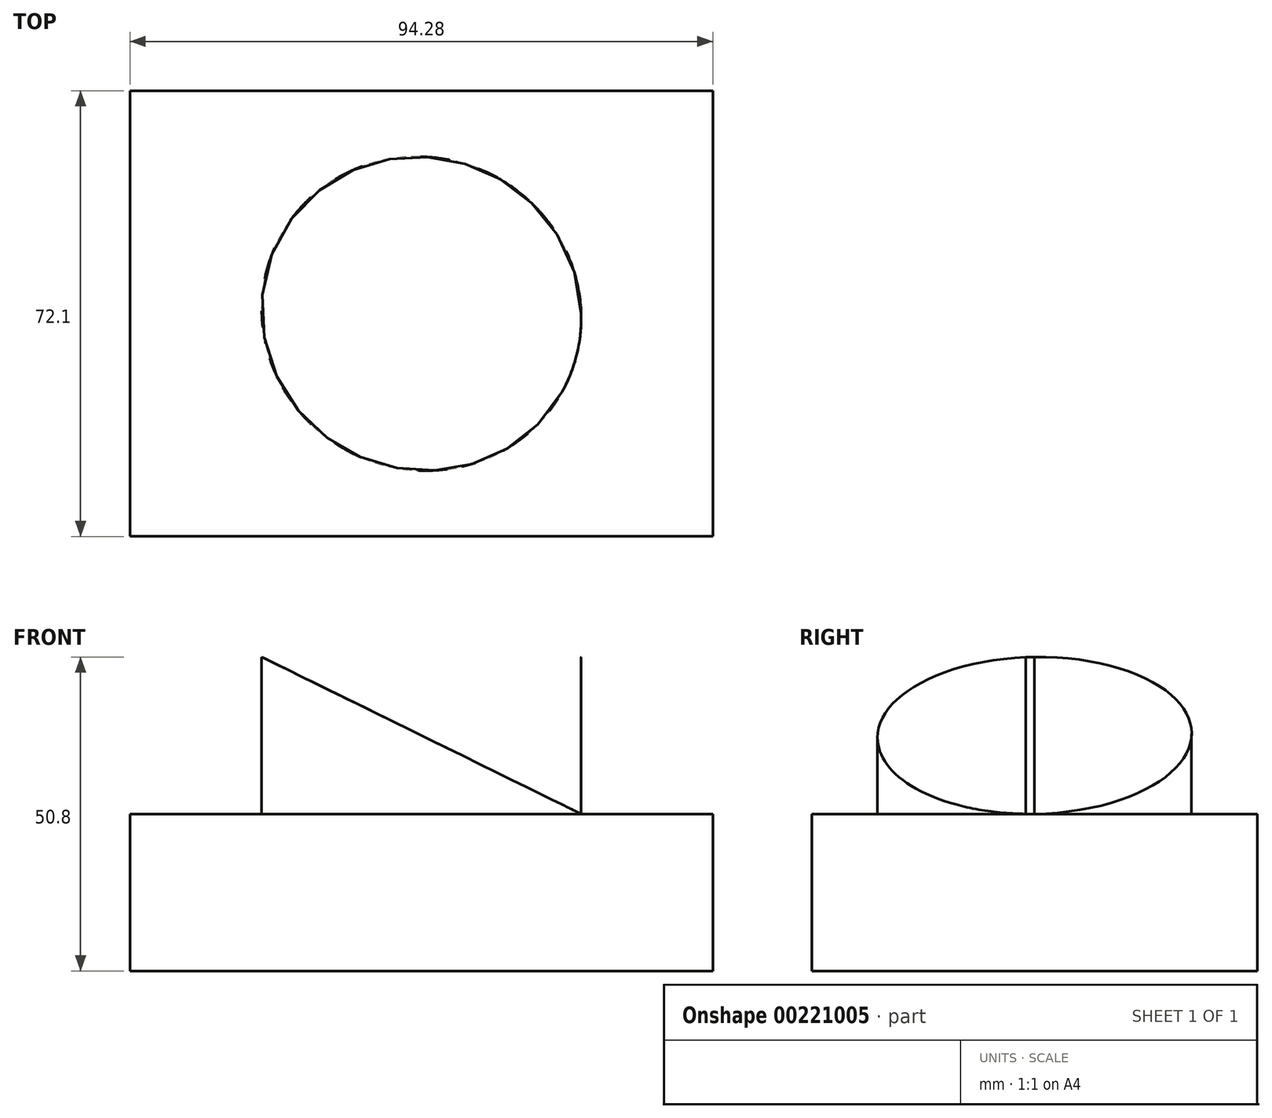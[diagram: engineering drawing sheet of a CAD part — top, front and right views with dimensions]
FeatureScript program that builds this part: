
annotation { "Feature Type Name" : "Feature", "Feature Type Description" : "" }
export const myFeature = defineFeature(function(context is Context, id is Id, definition is map)
    precondition{}
    {
        {
            var Q0;
            Q0=qCreatedBy(makeId("Top.planeOp"),FACE);
            var sketch = newSketch(context, id + "F0", { "sketchPlane" : qUnion([Q0])});
            skLineSegment(sketch, "E0.bottom", {"start": v(47.14, -36.05) * mm, "end": v(-47.14, -36.05) * mm});
            skLineSegment(sketch, "E0.top", {"start": v(47.14, 36.05) * mm, "end": v(-47.14, 36.05) * mm});
            skLineSegment(sketch, "E0.left", {"start": v(47.14, -36.05) * mm, "end": v(47.14, 36.05) * mm});
            skLineSegment(sketch, "E0.right", {"start": v(-47.14, -36.05) * mm, "end": v(-47.14, 36.05) * mm});
            skPoint(sketch, "E0.middle", {"position": v(0, 0) * mm});
            skSolve(sketch);
        }
        {
            var Q0;
            Q0 = qSketchRegion(id + "F0", true);
            extrude(context, id + "F1", {"entities" : qUnion([Q0]), "depth" : 25.4 * mm});
        }
        {
            var Q0;
            Q0=makeQuery(id+"F1.opExtrude","CAP_FACE",FACE,{"disambiguationData":[OSD([sQuery(id+"F0.wireOp",EDGE,"E0.bottom"),sQuery(id+"F0.wireOp",EDGE,"E0.top"),sQuery(id+"F0.wireOp",EDGE,"E0.left"),sQuery(id+"F0.wireOp",EDGE,"E0.right")])],"isStart":false});
            var sketch = newSketch(context, id + "F2", { "sketchPlane" : qUnion([Q0])});
            skEllipse(sketch, "E1", {"center": v(0, 0) * mm, "majorRadius": 26.04 * mm, "minorRadius": 25.2 * mm, "majorAxis": v(0.87, -0.49)});
            skSolve(sketch);
        }
        {
            var Q0;
            Q0 = qSketchRegion(id + "F2", true);
            extrude(context, id + "F3", {"entities" : qUnion([Q0]), "operationType" : NewBodyOperationType.ADD, "depth" : 25.4 * mm});
        }
        {
            var Q0;
            Q0=qCreatedBy(makeId("Front.planeOp"),FACE);
            var sketch = newSketch(context, id + "F4", { "sketchPlane" : qUnion([Q0])});
            skLineSegment(sketch, "E2.0", {"start": v(-25.85, 50.8) * mm, "end": v(25.85, 50.8) * mm});
            skLineSegment(sketch, "E3", {"start": v(25.85, 50.8) * mm, "end": v(25.85, 25.4) * mm});
            skLineSegment(sketch, "E4", {"start": v(-25.85, 50.8) * mm, "end": v(25.85, 25.4) * mm});
            skSolve(sketch);
        }
        {
            var Q0;
            Q0 = qSketchRegion(id + "F4", true);
            extrude(context, id + "F5", {"entities" : qUnion([Q0]), "operationType" : NewBodyOperationType.REMOVE, "endBound" : BoundingType.THROUGH_ALL, "oppositeDirection" : true, "depth" : 25.4 * mm});
        }
        {
            var Q0;
            Q0=qCreatedBy(makeId("Front.planeOp"),FACE);
            var sketch = newSketch(context, id + "F6", { "sketchPlane" : qUnion([Q0])});
            skLineSegment(sketch, "E5.0", {"start": v(-25.84, 50.8) * mm, "end": v(25.85, 50.8) * mm});
            skLineSegment(sketch, "E6.0", {"start": v(25.84, 25.4) * mm, "end": v(25.84, 50.8) * mm});
            skLineSegment(sketch, "E7", {"start": v(-25.84, 50.8) * mm, "end": v(25.84, 25.4) * mm});
            skSolve(sketch);
        }
        {
            var Q0;
            Q0 = qSketchRegion(id + "F6", true);
            extrude(context, id + "F7", {"entities" : qUnion([Q0]), "operationType" : NewBodyOperationType.REMOVE, "endBound" : BoundingType.THROUGH_ALL, "oppositeDirection" : true, "depth" : 25.4 * mm});
        }
        {
            var Q0;
            Q0=makeQuery(id+"F5.boolean.opBoolean","COPY",FACE,{"derivedFrom":makeQuery(id+"F5.opExtrude","CAP_FACE",FACE,{"disambiguationData":[OSD([sQuery(id+"F4.wireOp",EDGE,"E2.0"),sQuery(id+"F4.wireOp",EDGE,"E3"),sQuery(id+"F4.wireOp",EDGE,"E4")])],"isStart":true})});
            var sketch = newSketch(context, id + "F8", { "sketchPlane" : qUnion([Q0])});
            skLineSegment(sketch, "E8.0.0", {"start": v(25.84, 50.8) * mm, "end": v(25.84, 50.8) * mm});
            skLineSegment(sketch, "E8.0.1", {"start": v(25.84, 50.8) * mm, "end": v(-25.84, 50.8) * mm});
            skLineSegment(sketch, "E8.0.2", {"start": v(-25.84, 25.4) * mm, "end": v(-25.84, 50.8) * mm});
            skLineSegment(sketch, "E8.0.3", {"start": v(-25.84, 25.4) * mm, "end": v(25.84, 50.8) * mm});
            skSolve(sketch);
        }
        {
            var Q0;
            Q0 = qSketchRegion(id + "F8", true);
            extrude(context, id + "F9", {"entities" : qUnion([Q0]), "operationType" : NewBodyOperationType.REMOVE, "endBound" : BoundingType.THROUGH_ALL, "oppositeDirection" : true, "depth" : 25.4 * mm});
        }
    });
